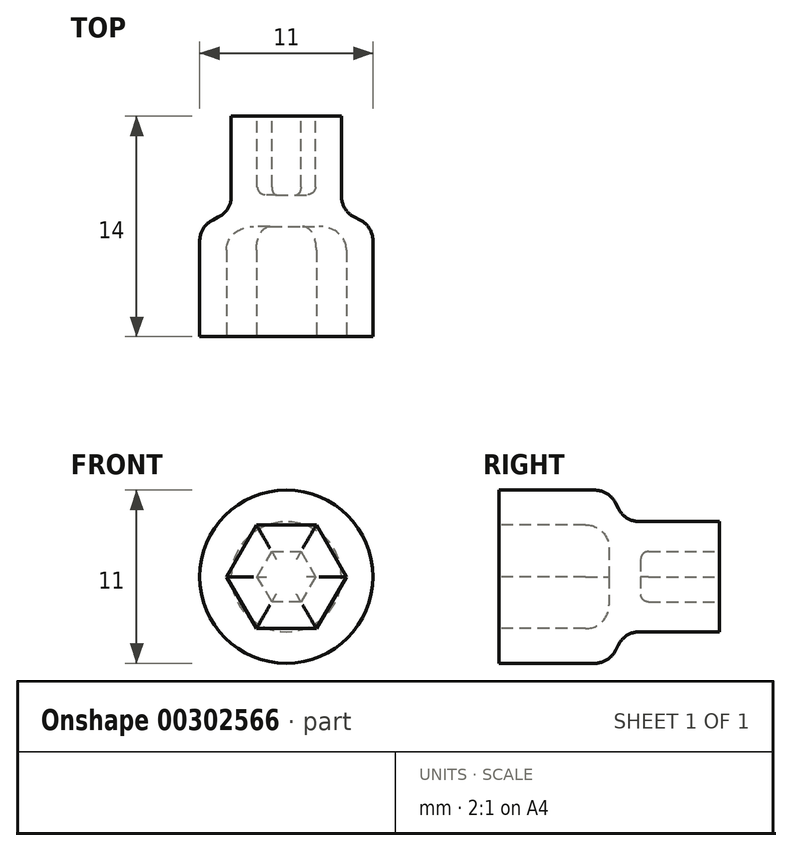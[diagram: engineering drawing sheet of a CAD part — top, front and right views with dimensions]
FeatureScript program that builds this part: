
annotation { "Feature Type Name" : "Feature", "Feature Type Description" : "" }
export const myFeature = defineFeature(function(context is Context, id is Id, definition is map)
    precondition{}
    {
        {
            var Q0;
            Q0=qCreatedBy(makeId("Top.planeOp"),FACE);
            var sketch = newSketch(context, id + "F0", { "sketchPlane" : qUnion([Q0])});
            skLineSegment(sketch, "E0", {"start": v(0, 10.48) * mm, "end": v(0, 0) * mm, "construction": true});
            skLineSegment(sketch, "E1", {"start": v(3.5, 7) * mm, "end": v(3.5, 1) * mm});
            skLineSegment(sketch, "E2", {"start": v(3.5, 1) * mm, "end": v(5.5, 0) * mm});
            skLineSegment(sketch, "E3", {"start": v(5.5, 0) * mm, "end": v(5.5, -7) * mm});
            skLineSegment(sketch, "E4", {"start": v(0, 7) * mm, "end": v(3.5, 7) * mm});
            skLineSegment(sketch, "E5", {"start": v(0, -7) * mm, "end": v(5.5, -7) * mm});
            skLineSegment(sketch, "E6.trimOffspring", {"start": v(0, -1.75) * mm, "end": v(0, -9.73) * mm, "construction": true});
            skLineSegment(sketch, "E7", {"start": v(0, -7) * mm, "end": v(0, 7) * mm});
            skSolve(sketch);
        }
        {
            var Q0;
            Q0=makeQuery(id+"F0.imprint","IMPRINT",FACE,{"disambiguationData":[TD([[makeQuery(id+"F0.imprint","IMPRINT",EDGE,{"derivedFrom":sQuery(id+"F0.wireOp",EDGE,"E1")}),-1.0]])]});
            var Q1;
            Q1=sQuery(id+"F0.wireOp",EDGE,"E6.trimOffspring");
            revolve(context, id + "F1", {"entities" : qUnion([Q0]), "axis" : qUnion([Q1]), "revolveType" : RevolveType.FULL});
        }
        {
            var Q0;
            Q0=makeQuery(id+"F1.opRevolve","SWEPT_FACE",FACE,{"disambiguationData":[OSD([sQuery(id+"F0.wireOp",EDGE,"E4")])]});
            var sketch = newSketch(context, id + "F2", { "sketchPlane" : qUnion([Q0])});
            skCircle(sketch, "E8", {"center": v(0, 0) * mm, "radius": 1.85 * mm});
            skLineSegment(sketch, "E9", {"start": v(-1.85, 0) * mm, "end": v(-0.92, -1.6) * mm});
            skLineSegment(sketch, "E10", {"start": v(-0.92, -1.6) * mm, "end": v(0.92, -1.6) * mm});
            skLineSegment(sketch, "E11", {"start": v(0.92, -1.6) * mm, "end": v(1.85, 0) * mm});
            skLineSegment(sketch, "E12", {"start": v(1.85, 0) * mm, "end": v(0.92, 1.6) * mm});
            skLineSegment(sketch, "E13", {"start": v(0.92, 1.6) * mm, "end": v(-0.92, 1.6) * mm});
            skLineSegment(sketch, "E14", {"start": v(-0.92, 1.6) * mm, "end": v(-1.85, 0) * mm});
            skSolve(sketch);
        }
        {
            var Q0;
            Q0=makeQuery(id+"F2.imprint","IMPRINT",FACE,{"disambiguationData":[TD([[makeQuery(id+"F2.imprint","IMPRINT",EDGE,{"derivedFrom":sQuery(id+"F2.wireOp",EDGE,"E9")}),1.0]])]});
            extrude(context, id + "F3", {"entities" : qUnion([Q0]), "operationType" : NewBodyOperationType.REMOVE, "oppositeDirection" : true, "depth" : 5 * mm});
        }
        {
            var Q0;
            Q0=makeQuery(id+"F1.opRevolve","SWEPT_FACE",FACE,{"disambiguationData":[OSD([sQuery(id+"F0.wireOp",EDGE,"E5")])]});
            var sketch = newSketch(context, id + "F4", { "sketchPlane" : qUnion([Q0])});
            skCircle(sketch, "E15", {"center": v(0, 0) * mm, "radius": 3.81 * mm});
            skLineSegment(sketch, "E16", {"start": v(3.81, 0) * mm, "end": v(1.9, 3.3) * mm});
            skLineSegment(sketch, "E17", {"start": v(1.9, 3.3) * mm, "end": v(-1.9, 3.3) * mm});
            skLineSegment(sketch, "E18", {"start": v(-1.9, 3.3) * mm, "end": v(-3.81, 0) * mm});
            skLineSegment(sketch, "E19", {"start": v(-3.81, 0) * mm, "end": v(-1.9, -3.3) * mm});
            skLineSegment(sketch, "E20", {"start": v(-1.9, -3.3) * mm, "end": v(1.9, -3.3) * mm});
            skLineSegment(sketch, "E21", {"start": v(1.9, -3.3) * mm, "end": v(3.81, 0) * mm});
            skSolve(sketch);
        }
        {
            var Q0;
            Q0=makeQuery(id+"F1.opRevolve","SWEPT_EDGE",EDGE,{"disambiguationData":[OSD([sQuery(id+"F0.wireOp",EDGE,"E2"),sQuery(id+"F0.wireOp",EDGE,"E3")])]});
            var Q1;
            Q1=makeQuery(id+"F1.opRevolve","SWEPT_EDGE",EDGE,{"disambiguationData":[OSD([sQuery(id+"F0.wireOp",EDGE,"E1"),sQuery(id+"F0.wireOp",EDGE,"E2")])]});
            fillet(context, id + "F5", {"entities" : qUnion([Q0, Q1]), "radius" : 1.5 * mm, "tangentPropagation" : true, "allowEdgeOverflow" : false});
        }
        {
            var Q0;
            Q0=makeQuery(id+"F4.imprint","IMPRINT",FACE,{"disambiguationData":[TD([[makeQuery(id+"F4.imprint","IMPRINT",EDGE,{"derivedFrom":sQuery(id+"F4.wireOp",EDGE,"E16")}),1.0]])]});
            extrude(context, id + "F6", {"entities" : qUnion([Q0]), "operationType" : NewBodyOperationType.REMOVE, "oppositeDirection" : true, "depth" : 7 * mm});
        }
        {
            var Q0;
            Q0=makeQuery(id+"F6.boolean.opBoolean","COPY",EDGE,{"derivedFrom":makeQuery(id+"F6.opExtrude","CAP_EDGE",EDGE,{"disambiguationData":[OSD([sQuery(id+"F4.wireOp",EDGE,"E20")])],"isStart":false})});
            var Q1;
            Q1=makeQuery(id+"F6.boolean.opBoolean","COPY",EDGE,{"derivedFrom":makeQuery(id+"F6.opExtrude","CAP_EDGE",EDGE,{"disambiguationData":[OSD([sQuery(id+"F4.wireOp",EDGE,"E21")])],"isStart":false})});
            var Q2;
            Q2=makeQuery(id+"F6.boolean.opBoolean","COPY",EDGE,{"derivedFrom":makeQuery(id+"F6.opExtrude","CAP_EDGE",EDGE,{"disambiguationData":[OSD([sQuery(id+"F4.wireOp",EDGE,"E16")])],"isStart":false})});
            var Q3;
            Q3=makeQuery(id+"F6.boolean.opBoolean","COPY",EDGE,{"derivedFrom":makeQuery(id+"F6.opExtrude","CAP_EDGE",EDGE,{"disambiguationData":[OSD([sQuery(id+"F4.wireOp",EDGE,"E17")])],"isStart":false})});
            var Q4;
            Q4=makeQuery(id+"F6.boolean.opBoolean","COPY",EDGE,{"derivedFrom":makeQuery(id+"F6.opExtrude","CAP_EDGE",EDGE,{"disambiguationData":[OSD([sQuery(id+"F4.wireOp",EDGE,"E18")])],"isStart":false})});
            var Q5;
            Q5=makeQuery(id+"F6.boolean.opBoolean","COPY",EDGE,{"derivedFrom":makeQuery(id+"F6.opExtrude","CAP_EDGE",EDGE,{"disambiguationData":[OSD([sQuery(id+"F4.wireOp",EDGE,"E19")])],"isStart":false})});
            fillet(context, id + "F7", {"entities" : qUnion([Q0, Q1, Q2, Q3, Q4, Q5]), "radius" : 1.5 * mm, "tangentPropagation" : true, "allowEdgeOverflow" : false});
        }
        {
            var Q0;
            Q0=makeQuery(id+"F3.boolean.opBoolean","COPY",EDGE,{"derivedFrom":makeQuery(id+"F3.opExtrude","CAP_EDGE",EDGE,{"disambiguationData":[OSD([sQuery(id+"F2.wireOp",EDGE,"E10")])],"isStart":false})});
            var Q1;
            Q1=makeQuery(id+"F3.boolean.opBoolean","COPY",EDGE,{"derivedFrom":makeQuery(id+"F3.opExtrude","CAP_EDGE",EDGE,{"disambiguationData":[OSD([sQuery(id+"F2.wireOp",EDGE,"E11")])],"isStart":false})});
            var Q2;
            Q2=makeQuery(id+"F3.boolean.opBoolean","COPY",EDGE,{"derivedFrom":makeQuery(id+"F3.opExtrude","CAP_EDGE",EDGE,{"disambiguationData":[OSD([sQuery(id+"F2.wireOp",EDGE,"E9")])],"isStart":false})});
            var Q3;
            Q3=makeQuery(id+"F3.boolean.opBoolean","COPY",EDGE,{"derivedFrom":makeQuery(id+"F3.opExtrude","CAP_EDGE",EDGE,{"disambiguationData":[OSD([sQuery(id+"F2.wireOp",EDGE,"E12")])],"isStart":false})});
            var Q4;
            Q4=makeQuery(id+"F3.boolean.opBoolean","COPY",EDGE,{"derivedFrom":makeQuery(id+"F3.opExtrude","CAP_EDGE",EDGE,{"disambiguationData":[OSD([sQuery(id+"F2.wireOp",EDGE,"E13")])],"isStart":false})});
            var Q5;
            Q5=makeQuery(id+"F3.boolean.opBoolean","COPY",EDGE,{"derivedFrom":makeQuery(id+"F3.opExtrude","CAP_EDGE",EDGE,{"disambiguationData":[OSD([sQuery(id+"F2.wireOp",EDGE,"E14")])],"isStart":false})});
            fillet(context, id + "F8", {"entities" : qUnion([Q0, Q1, Q2, Q3, Q4, Q5]), "radius" : 0.5 * mm, "tangentPropagation" : true, "allowEdgeOverflow" : false});
        }
    });
